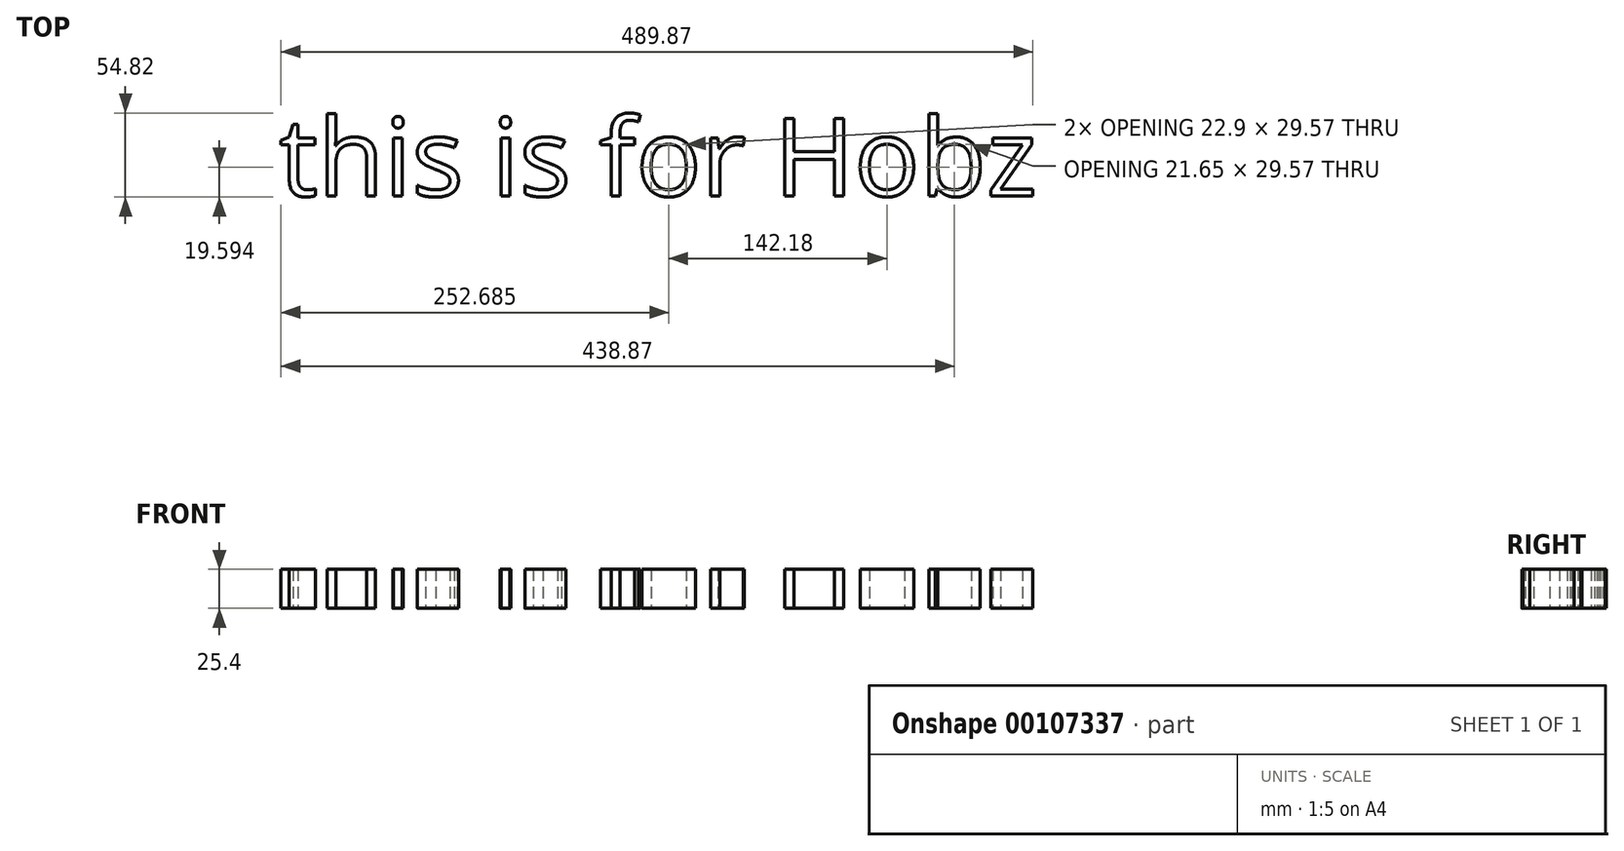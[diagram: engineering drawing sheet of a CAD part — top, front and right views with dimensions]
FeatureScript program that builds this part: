
annotation { "Feature Type Name" : "Feature", "Feature Type Description" : "" }
export const myFeature = defineFeature(function(context is Context, id is Id, definition is map)
    precondition{}
    {
        {
            var Q0;
            Q0=qCreatedBy(makeId("Top.planeOp"),FACE);
            var sketch = newSketch(context, id + "F0", { "sketchPlane" : qUnion([Q0])});
            skText(sketch, "E0", { "text": "this is for Hobz\n", "fontName": "OpenSans-Regular.ttf"});
            const initialGuessF0  = {"E0": [-0.05094, -0.03424, 1, 0, 0.05093]};
            skSetInitialGuess(sketch, initialGuessF0);
            skSolve(sketch);
        }
        {
            var Q0;
            Q0 = qSketchRegion(id + "F0", true);
            extrude(context, id + "F1", {"entities" : qUnion([Q0]), "depth" : 25.4 * mm});
        }
    });
